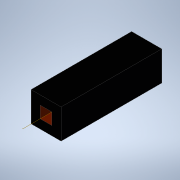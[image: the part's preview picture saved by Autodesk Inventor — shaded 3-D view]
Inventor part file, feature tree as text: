
AUTODESK INVENTOR PART (.ipt)
format: ipt  version: 2020 (Build 240168000, 168)  size: 98,816 bytes
history: native  units: in
note: dims shown in document units (in); Inventor stores cm internally (conversion verified against a paired STEP export)
features: other x2, plane x2
ambient origin geometry x8: Origin, YZ Plane, XZ Plane, XY Plane, X Axis, Y Axis, Z Axis, Center Point
bodies: Solid1 (feature_tree)
feature tree (4):
  other  "Work Axis1"
  plane  "Work Plane1"
  plane  "Work Plane2"
  other  "Part1"
